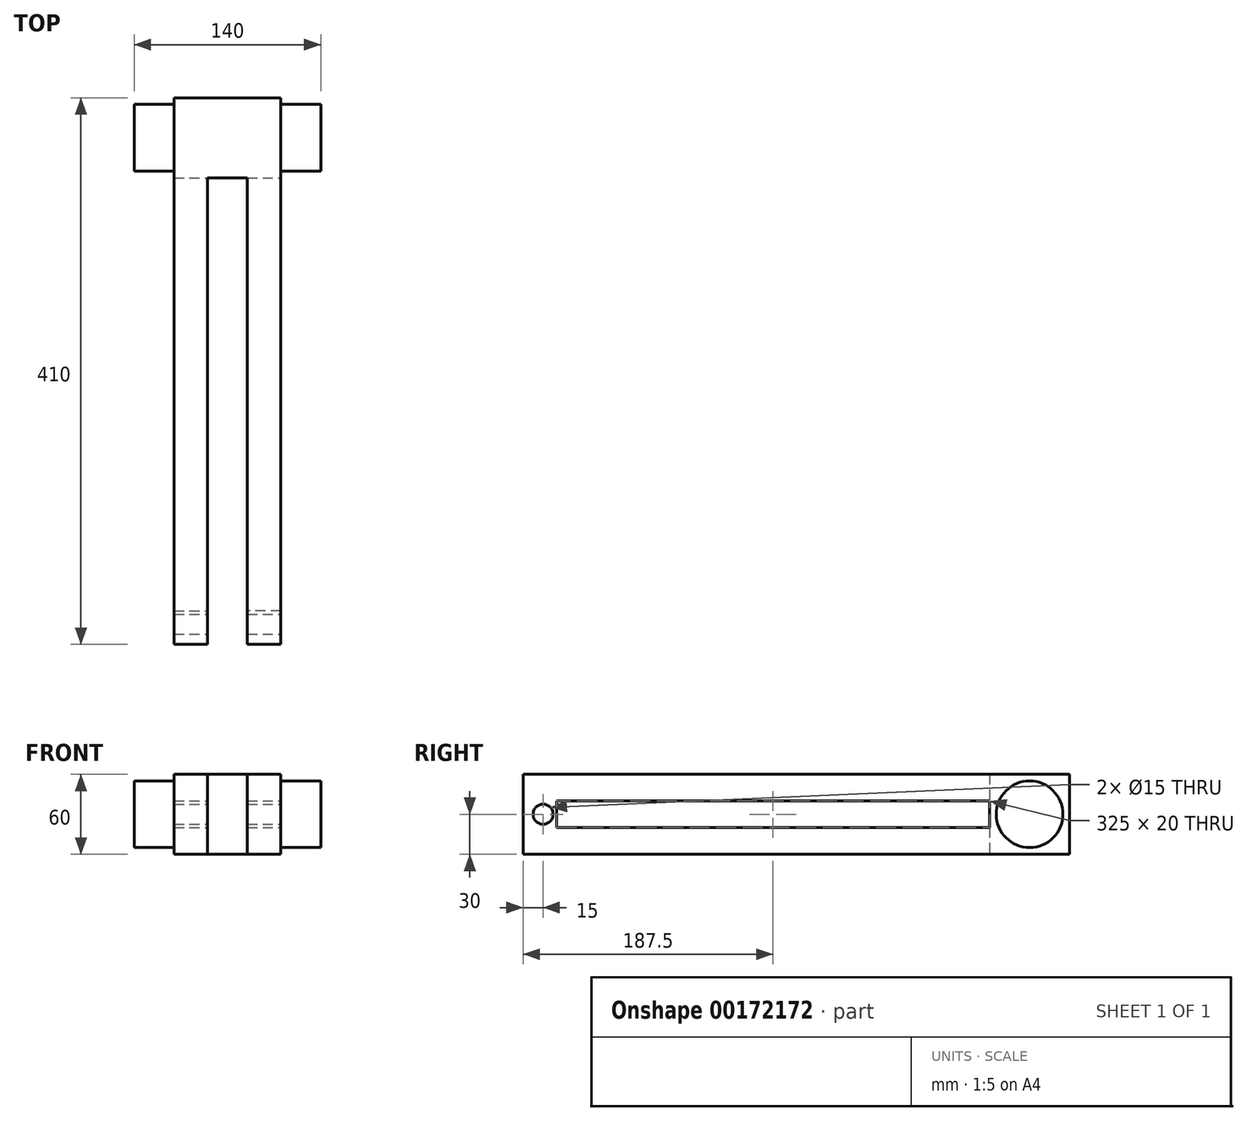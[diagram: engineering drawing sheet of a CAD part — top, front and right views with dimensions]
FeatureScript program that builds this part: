
annotation { "Feature Type Name" : "Feature", "Feature Type Description" : "" }
export const myFeature = defineFeature(function(context is Context, id is Id, definition is map)
    precondition{}
    {
        {
            var Q0;
            Q0=qCreatedBy(makeId("Right.planeOp"),FACE);
            var sketch = newSketch(context, id + "F0", { "sketchPlane" : qUnion([Q0])});
            skCircle(sketch, "E0", {"center": v(0, 0) * mm, "radius": 25 * mm});
            skSolve(sketch);
        }
        {
            var Q0;
            Q0 = qSketchRegion(id + "F0", true);
            extrude(context, id + "F1", {"entities" : qUnion([Q0]), "depth" : 140 * mm});
        }
        {
            var Q0;
            Q0=qCreatedBy(makeId("Front.planeOp"),FACE);
            var sketch = newSketch(context, id + "F2", { "sketchPlane" : qUnion([Q0])});
            skLineSegment(sketch, "E1.bottom", {"start": v(30, 30) * mm, "end": v(110, 30) * mm});
            skLineSegment(sketch, "E1.top", {"start": v(30, -30) * mm, "end": v(110, -30) * mm});
            skLineSegment(sketch, "E1.left", {"start": v(30, 30) * mm, "end": v(30, -30) * mm});
            skLineSegment(sketch, "E1.right", {"start": v(110, 30) * mm, "end": v(110, -30) * mm});
            skSolve(sketch);
        }
        {
            var Q0;
            Q0 = qSketchRegion(id + "F2", true);
            extrude(context, id + "F3", {"entities" : qUnion([Q0]), "operationType" : NewBodyOperationType.ADD, "depth" : 30 * mm, "hasSecondDirection" : true, "secondDirectionOppositeDirection" : true, "secondDirectionDepth" : 30 * mm});
        }
        {
            var Q0;
            Q0=makeQuery(id+"F3.opExtrude","CAP_FACE",FACE,{"disambiguationData":[OSD([sQuery(id+"F2.wireOp",EDGE,"E1.bottom"),sQuery(id+"F2.wireOp",EDGE,"E1.top"),sQuery(id+"F2.wireOp",EDGE,"E1.left"),sQuery(id+"F2.wireOp",EDGE,"E1.right")])],"isStart":false});
            var sketch = newSketch(context, id + "F4", { "sketchPlane" : qUnion([Q0])});
            skLineSegment(sketch, "E2.bottom", {"start": v(85, 30) * mm, "end": v(110, 30) * mm});
            skLineSegment(sketch, "E2.top", {"start": v(85, 10) * mm, "end": v(110, 10) * mm});
            skLineSegment(sketch, "E2.left", {"start": v(85, 30) * mm, "end": v(85, 10) * mm});
            skLineSegment(sketch, "E2.right", {"start": v(110, 30) * mm, "end": v(110, 10) * mm});
            skLineSegment(sketch, "E3.bottom", {"start": v(30, 30) * mm, "end": v(55, 30) * mm});
            skLineSegment(sketch, "E3.top", {"start": v(30, 10) * mm, "end": v(55, 10) * mm});
            skLineSegment(sketch, "E3.left", {"start": v(30, 30) * mm, "end": v(30, 10) * mm});
            skLineSegment(sketch, "E3.right", {"start": v(55, 30) * mm, "end": v(55, 10) * mm});
            skLineSegment(sketch, "E4.bottom", {"start": v(30, -10) * mm, "end": v(55, -10) * mm});
            skLineSegment(sketch, "E4.top", {"start": v(30, -30) * mm, "end": v(55, -30) * mm});
            skLineSegment(sketch, "E4.left", {"start": v(30, -10) * mm, "end": v(30, -30) * mm});
            skLineSegment(sketch, "E4.right", {"start": v(55, -10) * mm, "end": v(55, -30) * mm});
            skLineSegment(sketch, "E5.bottom", {"start": v(85, -10) * mm, "end": v(110, -10) * mm});
            skLineSegment(sketch, "E5.top", {"start": v(85, -30) * mm, "end": v(110, -30) * mm});
            skLineSegment(sketch, "E5.left", {"start": v(85, -10) * mm, "end": v(85, -30) * mm});
            skLineSegment(sketch, "E5.right", {"start": v(110, -10) * mm, "end": v(110, -30) * mm});
            skSolve(sketch);
        }
        {
            var Q0;
            Q0 = qSketchRegion(id + "F4", true);
            extrude(context, id + "F5", {"entities" : qUnion([Q0]), "operationType" : NewBodyOperationType.ADD, "depth" : 350 * mm});
        }
        {
            var Q0;
            Q0=makeQuery(id+"F5.boolean.opBoolean","MERGE",FACE,{"derivedFrom":[makeQuery(id+"F3.opExtrude","SWEPT_FACE",FACE,{"disambiguationData":[OSD([sQuery(id+"F2.wireOp",EDGE,"E1.bottom")])]}),makeQuery(id+"F5.opExtrude","SWEPT_FACE",FACE,{"disambiguationData":[OSD([sQuery(id+"F4.wireOp",EDGE,"E2.bottom")])]}),makeQuery(id+"F5.opExtrude","SWEPT_FACE",FACE,{"disambiguationData":[OSD([sQuery(id+"F4.wireOp",EDGE,"E3.bottom")])]})]});
            var sketch = newSketch(context, id + "F6", { "sketchPlane" : qUnion([Q0])});
            skLineSegment(sketch, "E6.bottom", {"start": v(110, -380) * mm, "end": v(85, -380) * mm});
            skLineSegment(sketch, "E6.top", {"start": v(110, -355) * mm, "end": v(85, -355) * mm});
            skLineSegment(sketch, "E6.left", {"start": v(110, -380) * mm, "end": v(110, -355) * mm});
            skLineSegment(sketch, "E6.right", {"start": v(85, -380) * mm, "end": v(85, -355) * mm});
            skLineSegment(sketch, "E7.bottom", {"start": v(30, -380) * mm, "end": v(55, -380) * mm});
            skLineSegment(sketch, "E7.top", {"start": v(30, -355) * mm, "end": v(55, -355) * mm});
            skLineSegment(sketch, "E7.left", {"start": v(30, -380) * mm, "end": v(30, -355) * mm});
            skLineSegment(sketch, "E7.right", {"start": v(55, -380) * mm, "end": v(55, -355) * mm});
            skSolve(sketch);
        }
        {
            var Q0;
            Q0 = qSketchRegion(id + "F6", true);
            extrude(context, id + "F7", {"entities" : qUnion([Q0]), "operationType" : NewBodyOperationType.ADD, "oppositeDirection" : true, "depth" : 50 * mm});
        }
        {
            var Q0;
            Q0=makeQuery(id+"F7.boolean.opBoolean","MERGE",FACE,{"derivedFrom":[makeQuery(id+"F5.boolean.opBoolean","MERGE",FACE,{"derivedFrom":[makeQuery(id+"F3.opExtrude","SWEPT_FACE",FACE,{"disambiguationData":[OSD([sQuery(id+"F2.wireOp",EDGE,"E1.right")])]}),makeQuery(id+"F5.opExtrude","SWEPT_FACE",FACE,{"disambiguationData":[OSD([sQuery(id+"F4.wireOp",EDGE,"E2.right")])]}),makeQuery(id+"F5.opExtrude","SWEPT_FACE",FACE,{"disambiguationData":[OSD([sQuery(id+"F4.wireOp",EDGE,"E5.right")])]})]}),makeQuery(id+"F7.opExtrude","SWEPT_FACE",FACE,{"disambiguationData":[OSD([sQuery(id+"F6.wireOp",EDGE,"E6.left")])]})]});
            var sketch = newSketch(context, id + "F8", { "sketchPlane" : qUnion([Q0])});
            skCircle(sketch, "E8", {"center": v(-365, 0) * mm, "radius": 7.5 * mm});
            skSolve(sketch);
        }
        {
            var Q0;
            Q0 = qSketchRegion(id + "F8", true);
            extrude(context, id + "F9", {"entities" : qUnion([Q0]), "operationType" : NewBodyOperationType.REMOVE, "endBound" : BoundingType.THROUGH_ALL, "oppositeDirection" : true, "depth" : 25 * mm});
        }
    });
